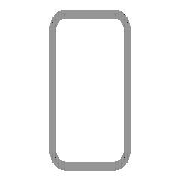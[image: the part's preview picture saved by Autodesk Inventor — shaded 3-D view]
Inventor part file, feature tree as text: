
AUTODESK INVENTOR PART (.ipt)
format: ipt  version: 2025.1 (Build 291241020, 241B)  size: 133,632 bytes
history: native  units: mm (DEFAULTED — no unit token found)
features: other x4, sketch x1, plane x1
ambient origin geometry x8: Origin, YZ Plane, XZ Plane, XY Plane, X Axis, Y Axis, Z Axis, Center Point
bodies: Solid1 (feature_tree), Body (feature_tree)
feature tree (6):
  parser-record x1  (decoder bookkeeping rows leaked as tree rows — omitted from the tree; the rows remain in map.json)
  other  "Driven Length"
  other  "Start Plane"
  other  "End Plane"
  sketch  "Sketch3"  dims[d3=4800.0mm d4=0.0mm d7=6.0mm d9=40.0mm d11=80.0mm d12=3.0mm d13=-0.0mm d14=4800.0mm d15=20.0mm d16=40.0mm d17=90.0deg d18=4800.0mm]
  plane  "Work Plane3"
